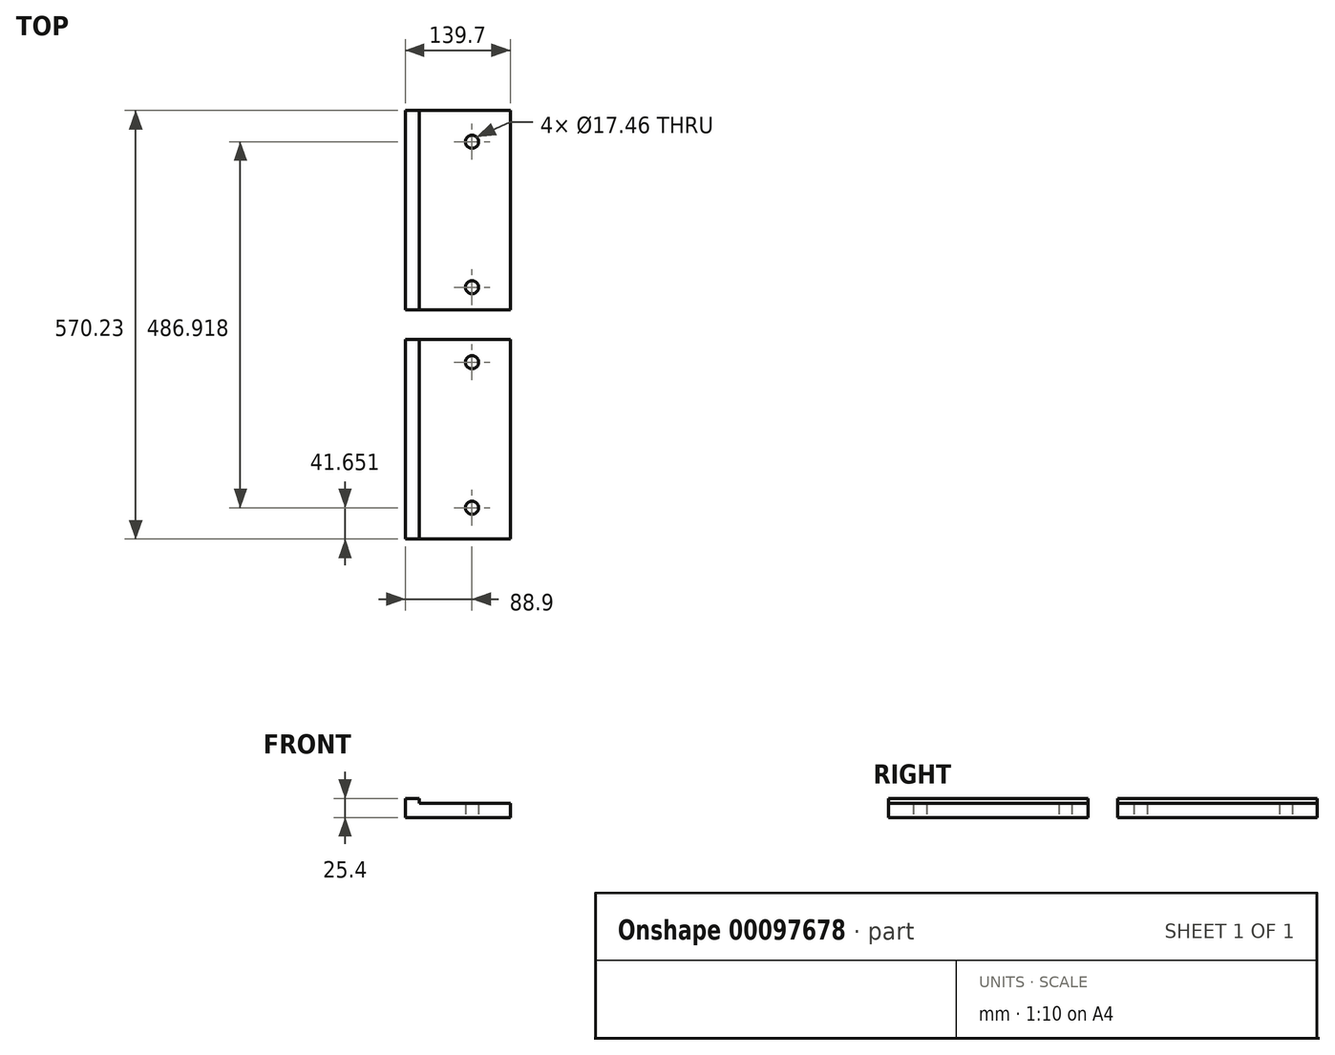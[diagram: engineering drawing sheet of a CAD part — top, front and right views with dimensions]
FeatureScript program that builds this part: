
annotation { "Feature Type Name" : "Feature", "Feature Type Description" : "" }
export const myFeature = defineFeature(function(context is Context, id is Id, definition is map)
    precondition{}
    {
        {
            var Q0;
            Q0=qCreatedBy(makeId("Top.planeOp"),FACE);
            var sketch = newSketch(context, id + "F0", { "sketchPlane" : qUnion([Q0])});
            skLineSegment(sketch, "E0.bottom", {"start": v(-69.85, 132.71) * mm, "end": v(69.85, 132.71) * mm});
            skLineSegment(sketch, "E0.top", {"start": v(-69.85, -132.72) * mm, "end": v(69.85, -132.72) * mm});
            skLineSegment(sketch, "E0.left", {"start": v(-69.85, 132.71) * mm, "end": v(-69.85, -132.72) * mm});
            skLineSegment(sketch, "E0.right", {"start": v(69.85, 132.71) * mm, "end": v(69.85, -132.72) * mm});
            skPoint(sketch, "E0.middle", {"position": v(0, 0) * mm});
            skLineSegment(sketch, "E1.0", {"start": v(-69.85, -5.72) * mm, "end": v(69.85, -5.72) * mm, "construction": true});
            skLineSegment(sketch, "E2.0", {"start": v(19.05, 132.71) * mm, "end": v(19.05, -132.72) * mm, "construction": true});
            skLineSegment(sketch, "E3.0", {"start": v(-69.85, 91.06) * mm, "end": v(69.85, 91.06) * mm, "construction": true});
            skCircle(sketch, "E4", {"center": v(19.05, 91.06) * mm, "radius": 8.73 * mm});
            skCircle(sketch, "E5.MirrorC", {"center": v(19.05, -102.49) * mm, "radius": 8.73 * mm});
            skSolve(sketch);
        }
        {
            var Q0;
            Q0=makeQuery(id+"F0.imprint","IMPRINT",FACE,{"disambiguationData":[TD([[makeQuery(id+"F0.imprint","IMPRINT",EDGE,{"derivedFrom":sQuery(id+"F0.wireOp",EDGE,"E0.bottom")}),-1.0]])]});
            extrude(context, id + "F1", {"entities" : qUnion([Q0]), "depth" : 19.05 * mm});
        }
        {
            var Q0;
            Q0=makeQuery(id+"F1.opExtrude","CAP_FACE",FACE,{"disambiguationData":[OSD([sQuery(id+"F0.wireOp",EDGE,"E0.bottom"),sQuery(id+"F0.wireOp",EDGE,"E0.top"),sQuery(id+"F0.wireOp",EDGE,"E0.left"),sQuery(id+"F0.wireOp",EDGE,"E0.right"),sQuery(id+"F0.wireOp",EDGE,"E4"),sQuery(id+"F0.wireOp",EDGE,"E5.MirrorC")])],"isStart":false});
            var sketch = newSketch(context, id + "F2", { "sketchPlane" : qUnion([Q0])});
            skLineSegment(sketch, "E6.bottom", {"start": v(-69.85, 132.71) * mm, "end": v(-50.8, 132.71) * mm});
            skLineSegment(sketch, "E6.top", {"start": v(-69.85, -132.72) * mm, "end": v(-50.8, -132.72) * mm});
            skLineSegment(sketch, "E6.left", {"start": v(-69.85, 132.71) * mm, "end": v(-69.85, -132.72) * mm});
            skLineSegment(sketch, "E6.right", {"start": v(-50.8, 132.71) * mm, "end": v(-50.8, -132.72) * mm});
            skSolve(sketch);
        }
        {
            var Q0;
            Q0 = qSketchRegion(id + "F2", true);
            extrude(context, id + "F3", {"entities" : qUnion([Q0]), "operationType" : NewBodyOperationType.ADD, "depth" : 6.35 * mm});
        }
        {
            var Q0;
            Q0=qCreatedBy(makeId("Front.planeOp"),FACE);
            cPlane(context, id + "F4", {"entities" : qUnion([Q0]), "cplaneType" : CPlaneType.OFFSET, "offset" : 152.4 * mm, "width" : 152.4 * mm, "height" : 152.4 * mm});
        }
        {
            var Q0;
            Q0=makeQuery(id+"F1.opExtrude","SWEPT_BODY",BODY,{"disambiguationData":[OSD([sQuery(id+"F0.wireOp",EDGE,"E0.bottom"),sQuery(id+"F0.wireOp",EDGE,"E0.top"),sQuery(id+"F0.wireOp",EDGE,"E0.left"),sQuery(id+"F0.wireOp",EDGE,"E0.right"),sQuery(id+"F0.wireOp",EDGE,"E4"),sQuery(id+"F0.wireOp",EDGE,"E5.MirrorC")])]});
            var Q1;
            Q1=qCreatedBy(id+"F4.planeOp",FACE);
            mirror(context, id + "F5", {"entities" : qUnion([Q0]), "mirrorPlane" : qUnion([Q1])});
        }
    });
